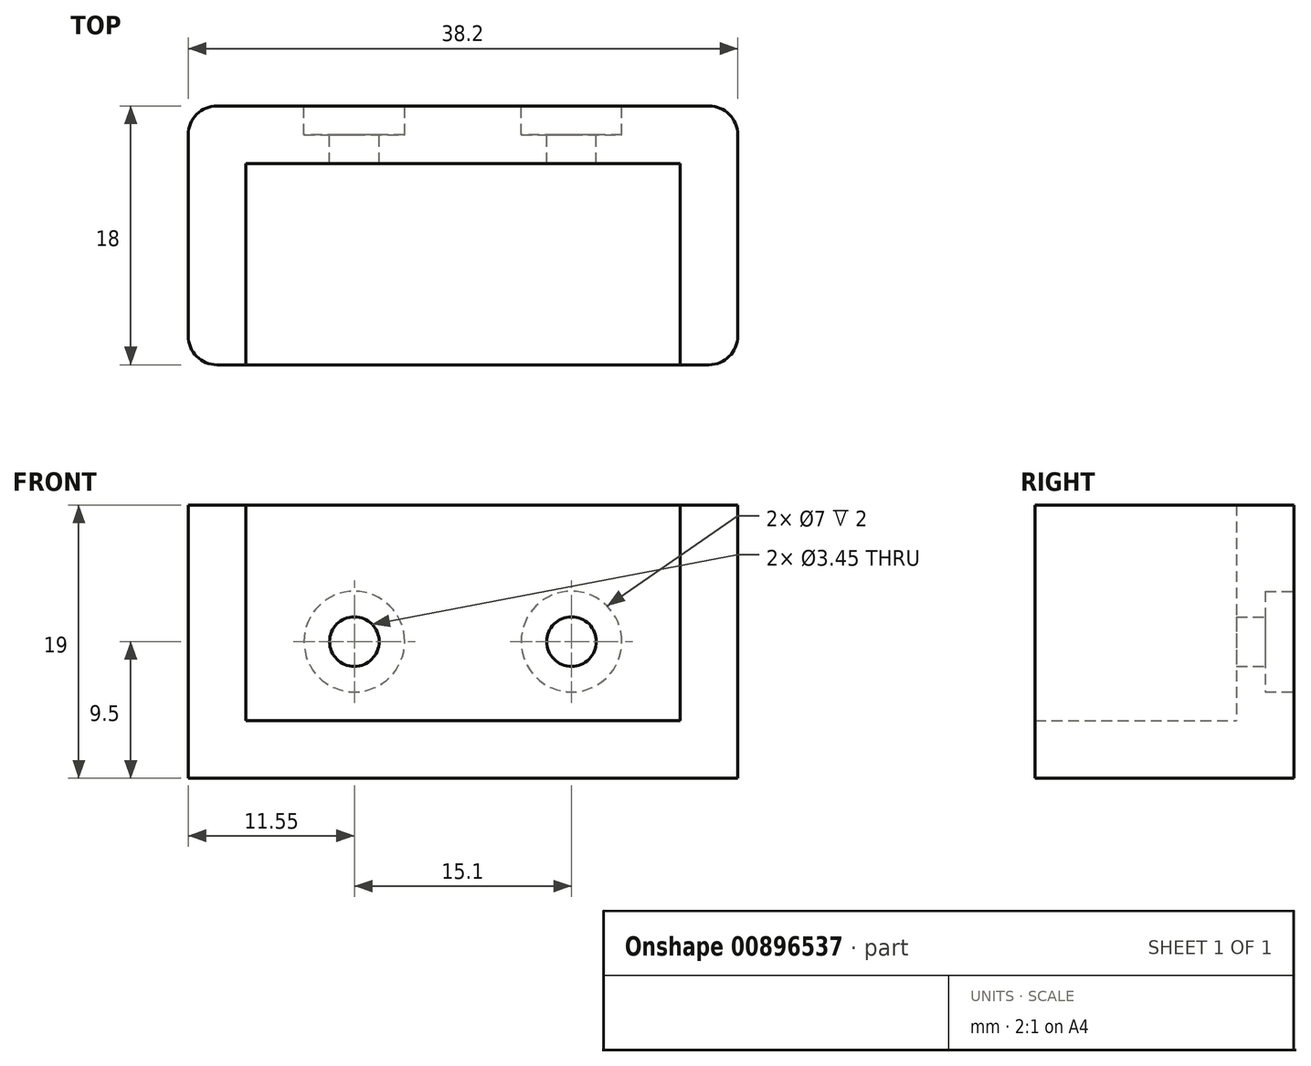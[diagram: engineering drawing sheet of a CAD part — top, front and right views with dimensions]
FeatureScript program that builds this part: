
annotation { "Feature Type Name" : "Feature", "Feature Type Description" : "" }
export const myFeature = defineFeature(function(context is Context, id is Id, definition is map)
    precondition{}
    {
        {
            var Q0;
            Q0=qCreatedBy(makeId("Top.planeOp"),FACE);
            var sketch = newSketch(context, id + "F0", { "sketchPlane" : qUnion([Q0])});
            skLineSegment(sketch, "E0.bottom", {"start": v(0, 0) * mm, "end": v(30.2, 0) * mm});
            skLineSegment(sketch, "E0.top", {"start": v(0, 14) * mm, "end": v(30.2, 14) * mm});
            skLineSegment(sketch, "E0.left", {"start": v(0, 0) * mm, "end": v(0, 14) * mm});
            skLineSegment(sketch, "E0.right", {"start": v(30.2, 0) * mm, "end": v(30.2, 14) * mm});
            skLineSegment(sketch, "E1", {"start": v(0, 0) * mm, "end": v(-4, 0) * mm});
            skLineSegment(sketch, "E2", {"start": v(-4, 0) * mm, "end": v(-4, 18) * mm});
            skLineSegment(sketch, "E3", {"start": v(-4, 18) * mm, "end": v(34.2, 18) * mm});
            skLineSegment(sketch, "E4", {"start": v(34.2, 18) * mm, "end": v(34.2, 0) * mm});
            skLineSegment(sketch, "E5", {"start": v(34.2, 0) * mm, "end": v(30.2, 0) * mm});
            skSolve(sketch);
        }
        {
            var Q0;
            Q0=makeQuery(id+"F0.imprint","IMPRINT",FACE,{"disambiguationData":[TD([[makeQuery(id+"F0.imprint","IMPRINT",EDGE,{"derivedFrom":sQuery(id+"F0.wireOp",EDGE,"E0.top")}),1.0]])]});
            extrude(context, id + "F1", {"entities" : qUnion([Q0]), "depth" : (15 + 4) * mm, "offsetDistance" : 25 * mm});
        }
        {
            var Q0;
            Q0 = qSketchRegion(id + "F0", true);
            extrude(context, id + "F2", {"entities" : qUnion([Q0]), "operationType" : NewBodyOperationType.ADD, "depth" : 4 * mm, "offsetDistance" : 25 * mm});
        }
        {
            var Q0;
            Q0=makeQuery(id+"F1.opExtrude","SWEPT_EDGE",EDGE,{"disambiguationData":[OSD([sQuery(id+"F0.wireOp",EDGE,"E2"),sQuery(id+"F0.wireOp",EDGE,"E3")])]});
            var Q1;
            Q1=makeQuery(id+"F1.opExtrude","SWEPT_EDGE",EDGE,{"disambiguationData":[OSD([sQuery(id+"F0.wireOp",EDGE,"E3"),sQuery(id+"F0.wireOp",EDGE,"E4")])]});
            var Q2;
            Q2=makeQuery(id+"F1.opExtrude","SWEPT_EDGE",EDGE,{"disambiguationData":[OSD([sQuery(id+"F0.wireOp",EDGE,"E4"),sQuery(id+"F0.wireOp",EDGE,"E5")])]});
            var Q3;
            Q3=makeQuery(id+"F1.opExtrude","SWEPT_EDGE",EDGE,{"disambiguationData":[OSD([sQuery(id+"F0.wireOp",EDGE,"E1"),sQuery(id+"F0.wireOp",EDGE,"E2")])]});
            fillet(context, id + "F3", {"entities" : qUnion([Q0, Q1, Q2, Q3]), "radius" : 2 * mm, "tangentPropagation" : true, "allowEdgeOverflow" : false});
        }
        {
            var Q0;
            Q0=makeQuery(id+"F1.opExtrude","SWEPT_FACE",FACE,{"disambiguationData":[OSD([sQuery(id+"F0.wireOp",EDGE,"E3")])]});
            var sketch = newSketch(context, id + "F4", { "sketchPlane" : qUnion([Q0])});
            skCircle(sketch, "E6", {"center": v(-22.65, 9.5) * mm, "radius": 1.73 * mm});
            skCircle(sketch, "E7", {"center": v(-7.55, 9.5) * mm, "radius": 1.73 * mm});
            skCircle(sketch, "E8", {"center": v(-7.55, 9.5) * mm, "radius": 3.5 * mm});
            skCircle(sketch, "E9", {"center": v(-22.65, 9.5) * mm, "radius": 3.5 * mm});
            skLineSegment(sketch, "E10", {"start": v(-22.65, 9.5) * mm, "end": v(-7.55, 9.5) * mm, "construction": true});
            skLineSegment(sketch, "E11", {"start": v(-15.1, 0) * mm, "end": v(-15.1, 9.5) * mm, "construction": true});
            skLineSegment(sketch, "E12", {"start": v(-7.55, 9.5) * mm, "end": v(2, 9.5) * mm, "construction": true});
            skSolve(sketch);
        }
        {
            var Q0;
            Q0 = qSketchRegion(id + "F4", true);
            extrude(context, id + "F5", {"entities" : qUnion([Q0]), "operationType" : NewBodyOperationType.REMOVE, "oppositeDirection" : true, "depth" : 2 * mm, "offsetDistance" : 25 * mm});
        }
        {
            var Q0;
            Q0=makeQuery(id+"F4.imprint","IMPRINT",FACE,{"disambiguationData":[TD([[makeQuery(id+"F4.imprint","IMPRINT",EDGE,{"derivedFrom":sQuery(id+"F4.wireOp",EDGE,"E6")}),1.0]])]});
            var Q1;
            Q1=makeQuery(id+"F4.imprint","IMPRINT",FACE,{"disambiguationData":[TD([[makeQuery(id+"F4.imprint","IMPRINT",EDGE,{"derivedFrom":sQuery(id+"F4.wireOp",EDGE,"E7")}),1.0]])]});
            extrude(context, id + "F6", {"entities" : qUnion([Q0, Q1]), "operationType" : NewBodyOperationType.REMOVE, "endBound" : BoundingType.UP_TO_NEXT, "oppositeDirection" : true, "depth" : 25 * mm, "offsetDistance" : 25 * mm});
        }
    });
